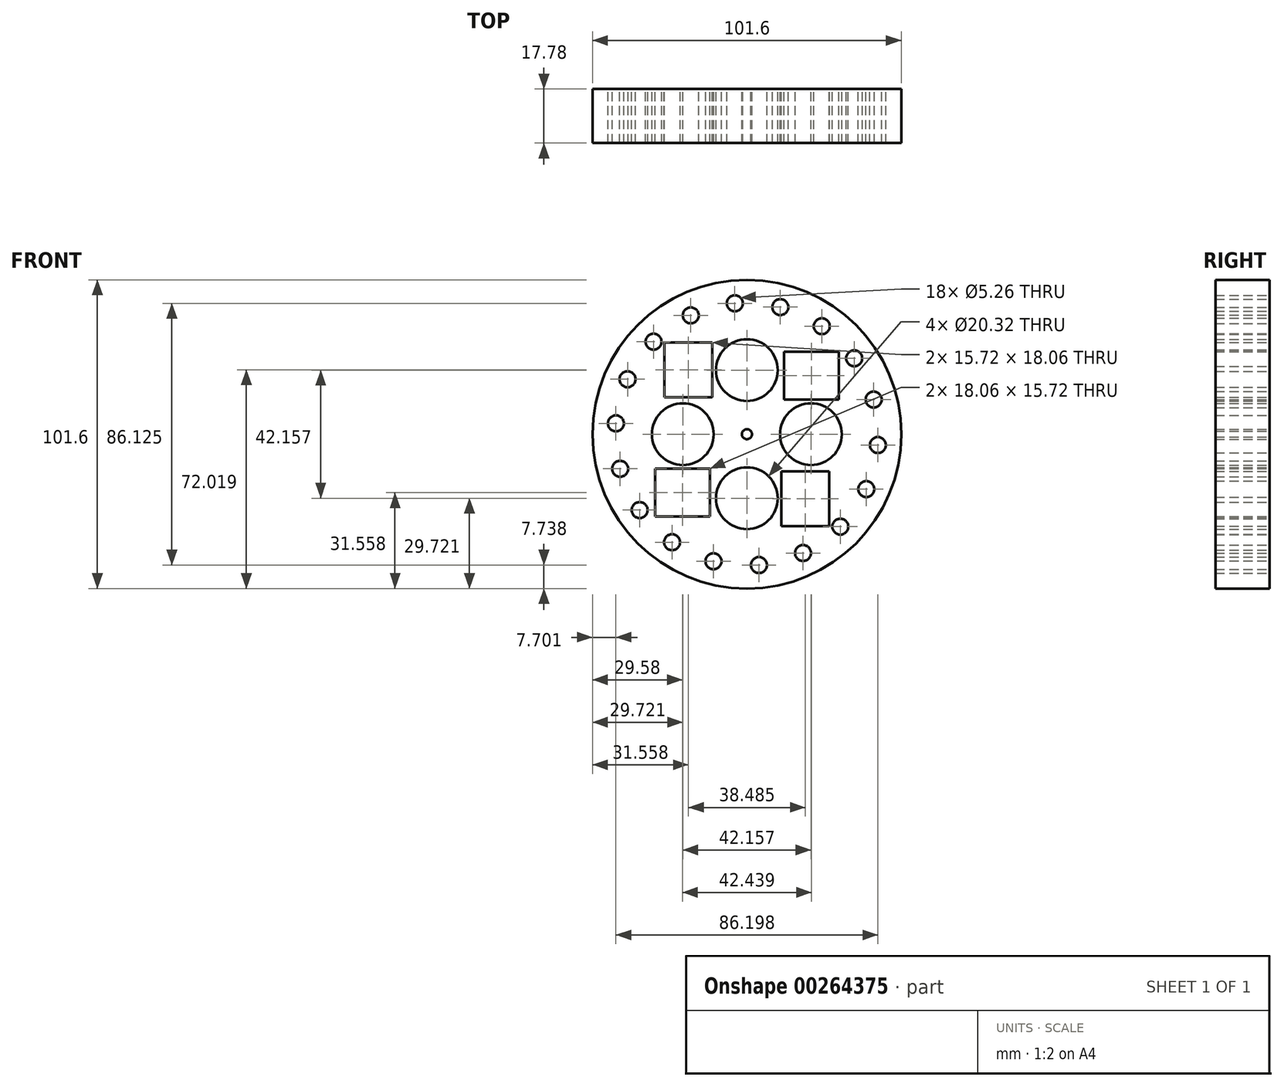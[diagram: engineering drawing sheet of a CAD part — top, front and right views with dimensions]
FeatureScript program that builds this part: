
annotation { "Feature Type Name" : "Feature", "Feature Type Description" : "" }
export const myFeature = defineFeature(function(context is Context, id is Id, definition is map)
    precondition{}
    {
        {
            var Q0;
            Q0=qCreatedBy(makeId("Front.planeOp"),FACE);
            var sketch = newSketch(context, id + "F0", { "sketchPlane" : qUnion([Q0])});
            skCircle(sketch, "E0", {"center": v(0, 0) * mm, "radius": 50.8 * mm});
            skCircle(sketch, "E1", {"center": v(0, 0) * mm, "radius": 1.65 * mm});
            skCircle(sketch, "E2", {"center": v(-30.73, 30.43) * mm, "radius": 2.63 * mm});
            skCircle(sketch, "E3.1.0", {"center": v(-39.28, 18.09) * mm, "radius": 2.63 * mm});
            skCircle(sketch, "E3.2.0", {"center": v(-43.1, 3.56) * mm, "radius": 2.63 * mm});
            skCircle(sketch, "E4.1.3.0", {"center": v(-41.72, -11.4) * mm, "radius": 2.63 * mm});
            skCircle(sketch, "E5.1.4.0", {"center": v(-35.3, -24.98) * mm, "radius": 2.63 * mm});
            skCircle(sketch, "E5.1.5.0", {"center": v(-24.63, -35.54) * mm, "radius": 2.63 * mm});
            skCircle(sketch, "E6.1.6.0", {"center": v(-10.99, -41.83) * mm, "radius": 2.63 * mm});
            skCircle(sketch, "E6.1.7.0", {"center": v(3.98, -43.06) * mm, "radius": 2.63 * mm});
            skCircle(sketch, "E7.1.8.0", {"center": v(18.47, -39.1) * mm, "radius": 2.63 * mm});
            skCircle(sketch, "E7.1.9.0", {"center": v(30.73, -30.43) * mm, "radius": 2.63 * mm});
            skCircle(sketch, "E7.1.10.0", {"center": v(39.28, -18.09) * mm, "radius": 2.63 * mm});
            skCircle(sketch, "E7.1.11.0", {"center": v(43.1, -3.56) * mm, "radius": 2.63 * mm});
            skCircle(sketch, "E8", {"center": v(-21.08, 0) * mm, "radius": 10.16 * mm});
            skCircle(sketch, "E9.1.0", {"center": v(0, -21.08) * mm, "radius": 10.16 * mm});
            skCircle(sketch, "E9.2.0", {"center": v(21.08, 0) * mm, "radius": 10.16 * mm});
            skCircle(sketch, "E9.3.0", {"center": v(0, 21.08) * mm, "radius": 10.16 * mm});
            skLineSegment(sketch, "E10.bottom", {"start": v(-11.38, 12.19) * mm, "end": v(-27.1, 12.19) * mm});
            skLineSegment(sketch, "E10.top", {"start": v(-11.38, 30.25) * mm, "end": v(-27.1, 30.25) * mm});
            skLineSegment(sketch, "E10.left", {"start": v(-11.38, 12.19) * mm, "end": v(-11.38, 30.25) * mm});
            skLineSegment(sketch, "E10.right", {"start": v(-27.1, 12.19) * mm, "end": v(-27.1, 30.25) * mm});
            skLineSegment(sketch, "E11.1.0", {"start": v(-12.19, -27.1) * mm, "end": v(-30.25, -27.1) * mm});
            skLineSegment(sketch, "E11.1.1", {"start": v(-12.19, -11.38) * mm, "end": v(-30.25, -11.38) * mm});
            skLineSegment(sketch, "E11.1.2", {"start": v(-12.19, -11.38) * mm, "end": v(-12.19, -27.1) * mm});
            skLineSegment(sketch, "E11.1.3", {"start": v(-30.25, -11.38) * mm, "end": v(-30.25, -27.1) * mm});
            skLineSegment(sketch, "E11.2.0", {"start": v(27.1, -12.19) * mm, "end": v(27.1, -30.25) * mm});
            skLineSegment(sketch, "E11.2.1", {"start": v(11.38, -12.19) * mm, "end": v(11.38, -30.25) * mm});
            skLineSegment(sketch, "E11.2.2", {"start": v(11.38, -12.19) * mm, "end": v(27.1, -12.19) * mm});
            skLineSegment(sketch, "E11.2.3", {"start": v(11.38, -30.25) * mm, "end": v(27.1, -30.25) * mm});
            skLineSegment(sketch, "E11.3.0", {"start": v(12.19, 27.1) * mm, "end": v(30.25, 27.1) * mm});
            skLineSegment(sketch, "E11.3.1", {"start": v(12.19, 11.38) * mm, "end": v(30.25, 11.38) * mm});
            skLineSegment(sketch, "E11.3.2", {"start": v(12.19, 11.38) * mm, "end": v(12.19, 27.1) * mm});
            skLineSegment(sketch, "E11.3.3", {"start": v(30.25, 11.38) * mm, "end": v(30.25, 27.1) * mm});
            skCircle(sketch, "E12.1.12.0", {"center": v(41.72, 11.4) * mm, "radius": 2.63 * mm});
            skCircle(sketch, "E12.1.13.0", {"center": v(35.3, 24.98) * mm, "radius": 2.63 * mm});
            skCircle(sketch, "E12.1.14.0", {"center": v(24.63, 35.54) * mm, "radius": 2.63 * mm});
            skCircle(sketch, "E12.1.15.0", {"center": v(10.99, 41.83) * mm, "radius": 2.63 * mm});
            skCircle(sketch, "E12.1.16.0", {"center": v(-3.98, 43.06) * mm, "radius": 2.63 * mm});
            skCircle(sketch, "E12.1.17.0", {"center": v(-18.47, 39.1) * mm, "radius": 2.63 * mm});
            skSolve(sketch);
        }
        {
            var Q0;
            Q0=makeQuery(id+"F0.imprint","IMPRINT",FACE,{"disambiguationData":[TD([[makeQuery(id+"F0.imprint","IMPRINT",EDGE,{"derivedFrom":sQuery(id+"F0.wireOp",EDGE,"E0")}),1.0]])]});
            extrude(context, id + "F1", {"entities" : qUnion([Q0]), "depth" : 17.78 * mm});
        }
    });
